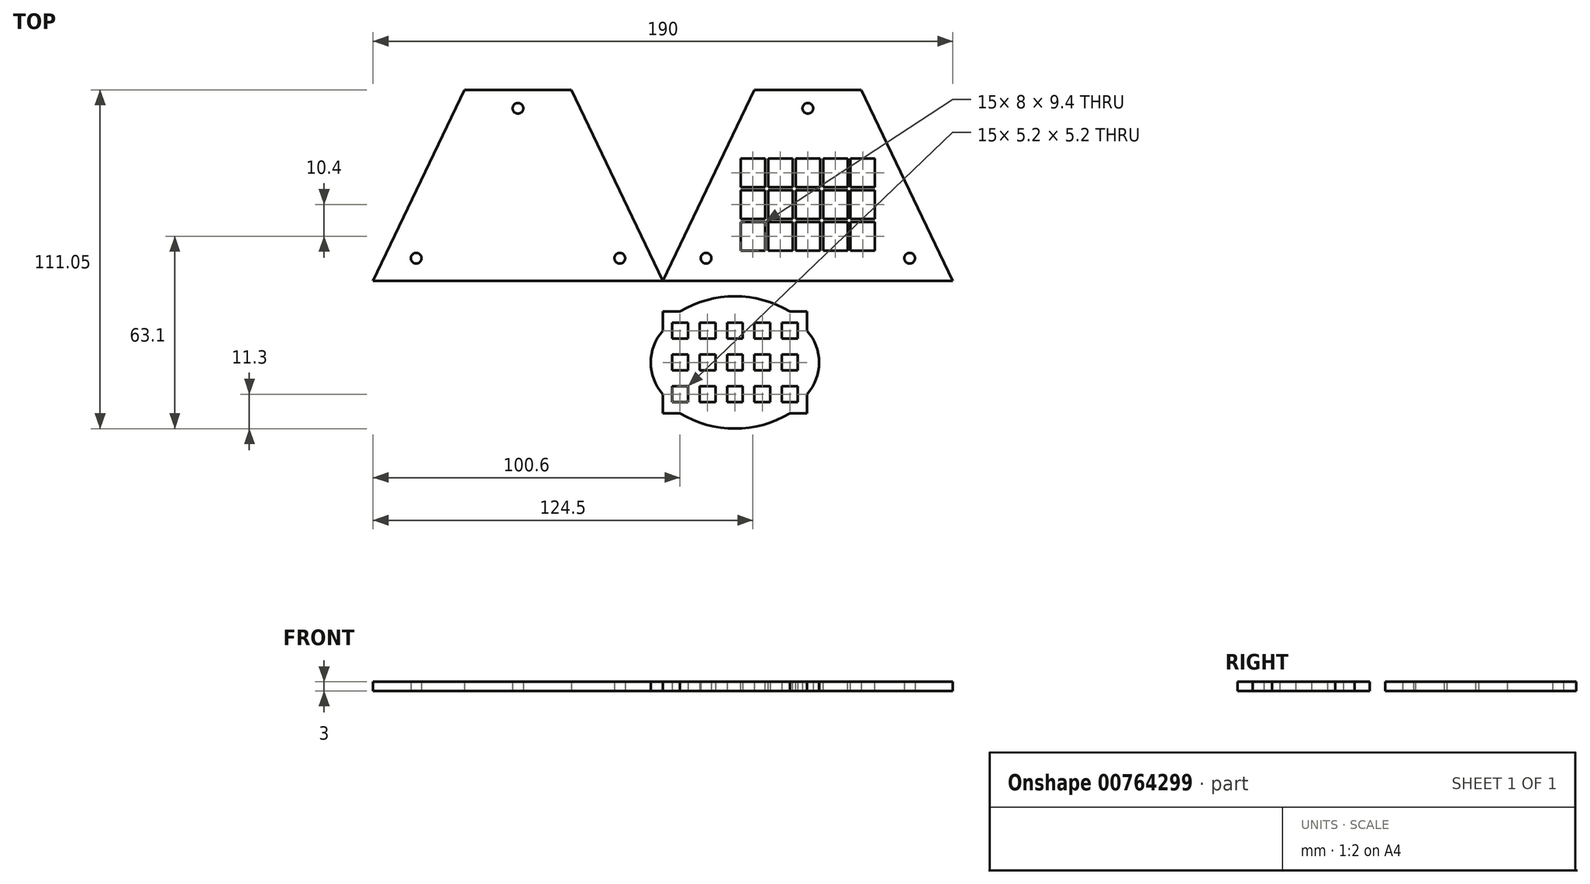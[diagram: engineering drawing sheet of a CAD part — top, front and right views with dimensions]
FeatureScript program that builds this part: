
annotation { "Feature Type Name" : "Feature", "Feature Type Description" : "" }
export const myFeature = defineFeature(function(context is Context, id is Id, definition is map)
    precondition{}
    {
        {
            var Q0;
            Q0=qCreatedBy(makeId("Top.planeOp"),FACE);
            var sketch = newSketch(context, id + "F0", { "sketchPlane" : qUnion([Q0])});
            skLineSegment(sketch, "E0", {"start": v(0, 0) * mm, "end": v(30, 62.65) * mm});
            skLineSegment(sketch, "E1", {"start": v(30, 62.65) * mm, "end": v(65, 62.65) * mm});
            skLineSegment(sketch, "E2", {"start": v(65, 62.65) * mm, "end": v(95, 0) * mm});
            skLineSegment(sketch, "E3", {"start": v(95, 0) * mm, "end": v(0, 0) * mm});
            skLineSegment(sketch, "E4", {"start": v(0, 0) * mm, "end": v(-95, 0) * mm});
            skLineSegment(sketch, "E5", {"start": v(-95, 0) * mm, "end": v(-65, 62.65) * mm});
            skLineSegment(sketch, "E6", {"start": v(-65, 62.65) * mm, "end": v(-30, 62.65) * mm});
            skLineSegment(sketch, "E7", {"start": v(-30, 62.65) * mm, "end": v(0, 0) * mm});
            skCircle(sketch, "E8", {"center": v(-80.86, 7.5) * mm, "radius": 1.75 * mm});
            skCircle(sketch, "E9", {"center": v(-14.14, 7.5) * mm, "radius": 1.75 * mm});
            skCircle(sketch, "E10", {"center": v(14.14, 7.5) * mm, "radius": 1.75 * mm});
            skCircle(sketch, "E11", {"center": v(80.86, 7.5) * mm, "radius": 1.75 * mm});
            skLineSegment(sketch, "E12", {"start": v(-95, 0) * mm, "end": v(-80.86, 7.5) * mm, "construction": true});
            skLineSegment(sketch, "E13", {"start": v(-80.86, 7.5) * mm, "end": v(-14.14, 7.5) * mm, "construction": true});
            skLineSegment(sketch, "E14", {"start": v(-14.14, 7.5) * mm, "end": v(0, 0) * mm, "construction": true});
            skLineSegment(sketch, "E15", {"start": v(0, 0) * mm, "end": v(14.14, 7.5) * mm, "construction": true});
            skLineSegment(sketch, "E16", {"start": v(14.14, 7.5) * mm, "end": v(80.86, 7.5) * mm, "construction": true});
            skLineSegment(sketch, "E17", {"start": v(80.86, 7.5) * mm, "end": v(95, 0) * mm, "construction": true});
            skLineSegment(sketch, "E18", {"start": v(-87.83, 14.98) * mm, "end": v(-80.86, 7.5) * mm, "construction": true});
            skLineSegment(sketch, "E19", {"start": v(-80.86, 7.5) * mm, "end": v(-73.9, 0) * mm, "construction": true});
            skCircle(sketch, "E20", {"center": v(-47.5, 56.65) * mm, "radius": 1.75 * mm});
            skCircle(sketch, "E21", {"center": v(47.5, 56.65) * mm, "radius": 1.75 * mm});
            skLineSegment(sketch, "E22", {"start": v(-47.5, 62.65) * mm, "end": v(-47.5, 56.65) * mm, "construction": true});
            skLineSegment(sketch, "E23", {"start": v(47.5, 62.65) * mm, "end": v(47.5, 56.65) * mm, "construction": true});
            skLineSegment(sketch, "E24.bottom", {"start": v(0, -10) * mm, "end": v(47.2, -10) * mm});
            skLineSegment(sketch, "E24.top", {"start": v(0, -43.4) * mm, "end": v(47.2, -43.4) * mm});
            skLineSegment(sketch, "E24.left", {"start": v(0, -10) * mm, "end": v(0, -43.4) * mm});
            skLineSegment(sketch, "E24.right", {"start": v(47.2, -10) * mm, "end": v(47.2, -43.4) * mm});
            skLineSegment(sketch, "E25.bottom", {"start": v(3, -39.7) * mm, "end": v(8.2, -39.7) * mm});
            skLineSegment(sketch, "E25.top", {"start": v(3, -34.5) * mm, "end": v(8.2, -34.5) * mm});
            skLineSegment(sketch, "E25.left", {"start": v(3, -39.7) * mm, "end": v(3, -34.5) * mm});
            skLineSegment(sketch, "E25.right", {"start": v(8.2, -39.7) * mm, "end": v(8.2, -34.5) * mm});
            skLineSegment(sketch, "E26.0.1.0", {"start": v(3, -29.3) * mm, "end": v(3, -24.1) * mm});
            skLineSegment(sketch, "E26.0.1.1", {"start": v(3, -24.1) * mm, "end": v(8.2, -24.1) * mm});
            skLineSegment(sketch, "E26.0.1.2", {"start": v(8.2, -29.3) * mm, "end": v(8.2, -24.1) * mm});
            skLineSegment(sketch, "E26.0.1.3", {"start": v(3, -29.3) * mm, "end": v(8.2, -29.3) * mm});
            skLineSegment(sketch, "E26.0.2.0", {"start": v(3, -18.9) * mm, "end": v(3, -13.7) * mm});
            skLineSegment(sketch, "E26.0.2.1", {"start": v(3, -13.7) * mm, "end": v(8.2, -13.7) * mm});
            skLineSegment(sketch, "E26.0.2.2", {"start": v(8.2, -18.9) * mm, "end": v(8.2, -13.7) * mm});
            skLineSegment(sketch, "E26.0.2.3", {"start": v(3, -18.9) * mm, "end": v(8.2, -18.9) * mm});
            skLineSegment(sketch, "E26.1.0.0", {"start": v(12, -39.7) * mm, "end": v(12, -34.5) * mm});
            skLineSegment(sketch, "E26.1.0.1", {"start": v(12, -34.5) * mm, "end": v(17.2, -34.5) * mm});
            skLineSegment(sketch, "E26.1.0.2", {"start": v(17.2, -39.7) * mm, "end": v(17.2, -34.5) * mm});
            skLineSegment(sketch, "E26.1.0.3", {"start": v(12, -39.7) * mm, "end": v(17.2, -39.7) * mm});
            skLineSegment(sketch, "E26.1.1.0", {"start": v(12, -29.3) * mm, "end": v(12, -24.1) * mm});
            skLineSegment(sketch, "E26.1.1.1", {"start": v(12, -24.1) * mm, "end": v(17.2, -24.1) * mm});
            skLineSegment(sketch, "E26.1.1.2", {"start": v(17.2, -29.3) * mm, "end": v(17.2, -24.1) * mm});
            skLineSegment(sketch, "E26.1.1.3", {"start": v(12, -29.3) * mm, "end": v(17.2, -29.3) * mm});
            skLineSegment(sketch, "E26.1.2.0", {"start": v(12, -18.9) * mm, "end": v(12, -13.7) * mm});
            skLineSegment(sketch, "E26.1.2.1", {"start": v(12, -13.7) * mm, "end": v(17.2, -13.7) * mm});
            skLineSegment(sketch, "E26.1.2.2", {"start": v(17.2, -18.9) * mm, "end": v(17.2, -13.7) * mm});
            skLineSegment(sketch, "E26.1.2.3", {"start": v(12, -18.9) * mm, "end": v(17.2, -18.9) * mm});
            skLineSegment(sketch, "E26.2.0.0", {"start": v(21, -39.7) * mm, "end": v(21, -34.5) * mm});
            skLineSegment(sketch, "E26.2.0.1", {"start": v(21, -34.5) * mm, "end": v(26.2, -34.5) * mm});
            skLineSegment(sketch, "E26.2.0.2", {"start": v(26.2, -39.7) * mm, "end": v(26.2, -34.5) * mm});
            skLineSegment(sketch, "E26.2.0.3", {"start": v(21, -39.7) * mm, "end": v(26.2, -39.7) * mm});
            skLineSegment(sketch, "E26.2.1.0", {"start": v(21, -29.3) * mm, "end": v(21, -24.1) * mm});
            skLineSegment(sketch, "E26.2.1.1", {"start": v(21, -24.1) * mm, "end": v(26.2, -24.1) * mm});
            skLineSegment(sketch, "E26.2.1.2", {"start": v(26.2, -29.3) * mm, "end": v(26.2, -24.1) * mm});
            skLineSegment(sketch, "E26.2.1.3", {"start": v(21, -29.3) * mm, "end": v(26.2, -29.3) * mm});
            skLineSegment(sketch, "E26.2.2.0", {"start": v(21, -18.9) * mm, "end": v(21, -13.7) * mm});
            skLineSegment(sketch, "E26.2.2.1", {"start": v(21, -13.7) * mm, "end": v(26.2, -13.7) * mm});
            skLineSegment(sketch, "E26.2.2.2", {"start": v(26.2, -18.9) * mm, "end": v(26.2, -13.7) * mm});
            skLineSegment(sketch, "E26.2.2.3", {"start": v(21, -18.9) * mm, "end": v(26.2, -18.9) * mm});
            skLineSegment(sketch, "E26.3.0.0", {"start": v(30, -39.7) * mm, "end": v(30, -34.5) * mm});
            skLineSegment(sketch, "E26.3.0.1", {"start": v(30, -34.5) * mm, "end": v(35.2, -34.5) * mm});
            skLineSegment(sketch, "E26.3.0.2", {"start": v(35.2, -39.7) * mm, "end": v(35.2, -34.5) * mm});
            skLineSegment(sketch, "E26.3.0.3", {"start": v(30, -39.7) * mm, "end": v(35.2, -39.7) * mm});
            skLineSegment(sketch, "E26.3.1.0", {"start": v(30, -29.3) * mm, "end": v(30, -24.1) * mm});
            skLineSegment(sketch, "E26.3.1.1", {"start": v(30, -24.1) * mm, "end": v(35.2, -24.1) * mm});
            skLineSegment(sketch, "E26.3.1.2", {"start": v(35.2, -29.3) * mm, "end": v(35.2, -24.1) * mm});
            skLineSegment(sketch, "E26.3.1.3", {"start": v(30, -29.3) * mm, "end": v(35.2, -29.3) * mm});
            skLineSegment(sketch, "E26.3.2.0", {"start": v(30, -18.9) * mm, "end": v(30, -13.7) * mm});
            skLineSegment(sketch, "E26.3.2.1", {"start": v(30, -13.7) * mm, "end": v(35.2, -13.7) * mm});
            skLineSegment(sketch, "E26.3.2.2", {"start": v(35.2, -18.9) * mm, "end": v(35.2, -13.7) * mm});
            skLineSegment(sketch, "E26.3.2.3", {"start": v(30, -18.9) * mm, "end": v(35.2, -18.9) * mm});
            skLineSegment(sketch, "E26.4.0.0", {"start": v(39, -39.7) * mm, "end": v(39, -34.5) * mm});
            skLineSegment(sketch, "E26.4.0.1", {"start": v(39, -34.5) * mm, "end": v(44.2, -34.5) * mm});
            skLineSegment(sketch, "E26.4.0.2", {"start": v(44.2, -39.7) * mm, "end": v(44.2, -34.5) * mm});
            skLineSegment(sketch, "E26.4.0.3", {"start": v(39, -39.7) * mm, "end": v(44.2, -39.7) * mm});
            skLineSegment(sketch, "E26.4.1.0", {"start": v(39, -29.3) * mm, "end": v(39, -24.1) * mm});
            skLineSegment(sketch, "E26.4.1.1", {"start": v(39, -24.1) * mm, "end": v(44.2, -24.1) * mm});
            skLineSegment(sketch, "E26.4.1.2", {"start": v(44.2, -29.3) * mm, "end": v(44.2, -24.1) * mm});
            skLineSegment(sketch, "E26.4.1.3", {"start": v(39, -29.3) * mm, "end": v(44.2, -29.3) * mm});
            skLineSegment(sketch, "E26.4.2.0", {"start": v(39, -18.9) * mm, "end": v(39, -13.7) * mm});
            skLineSegment(sketch, "E26.4.2.1", {"start": v(39, -13.7) * mm, "end": v(44.2, -13.7) * mm});
            skLineSegment(sketch, "E26.4.2.2", {"start": v(44.2, -18.9) * mm, "end": v(44.2, -13.7) * mm});
            skLineSegment(sketch, "E26.4.2.3", {"start": v(39, -18.9) * mm, "end": v(44.2, -18.9) * mm});
            skLineSegment(sketch, "E26.direction1", {"start": v(3, -39.7) * mm, "end": v(12, -39.7) * mm, "construction": true});
            skLineSegment(sketch, "E26.direction2", {"start": v(3, -39.7) * mm, "end": v(3, -29.3) * mm, "construction": true});
            skLineSegment(sketch, "E27", {"start": v(23.6, -39.7) * mm, "end": v(23.6, -43.4) * mm, "construction": true});
            skLineSegment(sketch, "E28", {"start": v(0, -26.7) * mm, "end": v(3, -26.7) * mm, "construction": true});
            skArc(sketch, "E29", {"start": v(41.6, -10) * mm, "mid": v(23.6, -5) * mm, "end": v(5.6, -10) * mm});
            skArc(sketch, "E30", {"start": v(5.6, -43.4) * mm, "mid": v(23.6, -48.4) * mm, "end": v(41.6, -43.4) * mm});
            skArc(sketch, "E31", {"start": v(47.2, -37.1) * mm, "mid": v(51.2, -26.7) * mm, "end": v(47.2, -16.3) * mm});
            skArc(sketch, "E32", {"start": v(0, -16.3) * mm, "mid": v(-4, -26.7) * mm, "end": v(0, -37.1) * mm});
            skLineSegment(sketch, "E33", {"start": v(0, -16.3) * mm, "end": v(3, -16.3) * mm, "construction": true});
            skLineSegment(sketch, "E34", {"start": v(5.6, -13.7) * mm, "end": v(5.6, -10) * mm, "construction": true});
            skLineSegment(sketch, "E35", {"start": v(11.52, -26.7) * mm, "end": v(23.6, -26.7) * mm, "construction": true});
            skLineSegment(sketch, "E36", {"start": v(23.6, -26.7) * mm, "end": v(35.68, -26.7) * mm, "construction": true});
            skLineSegment(sketch, "E37", {"start": v(41.6, -13.7) * mm, "end": v(41.6, -10) * mm, "construction": true});
            skLineSegment(sketch, "E38", {"start": v(0, -37.1) * mm, "end": v(3, -37.1) * mm, "construction": true});
            skPoint(sketch, "E39", {"position": v(23.6, -18.9) * mm});
            skLineSegment(sketch, "E40", {"start": v(23.6, -13.5) * mm, "end": v(23.6, -26.7) * mm, "construction": true});
            skLineSegment(sketch, "E41", {"start": v(23.6, -26.7) * mm, "end": v(23.6, -39.9) * mm, "construction": true});
            skSolve(sketch);
        }
        {
            var Q0;
            Q0=makeQuery(id+"F0.imprint","IMPRINT",FACE,{"disambiguationData":[TD([[makeQuery(id+"F0.imprint","IMPRINT",EDGE,{"derivedFrom":sQuery(id+"F0.wireOp",EDGE,"E4")}),-1.0]])]});
            var Q1;
            Q1=makeQuery(id+"F0.imprint","IMPRINT",FACE,{"disambiguationData":[TD([[makeQuery(id+"F0.imprint","IMPRINT",EDGE,{"derivedFrom":sQuery(id+"F0.wireOp",EDGE,"E0")}),-1.0]])]});
            var Q2;
            Q2=makeQuery(id+"F0.imprint","IMPRINT",FACE,{"disambiguationData":[TD([[makeQuery(id+"F0.imprint","IMPRINT",EDGE,{"derivedFrom":sQuery(id+"F0.wireOp",EDGE,"E24.bottom")}),-1.0]])]});
            var Q3;
            {var subQ0=sQuery(id+"F0.wireOp",EDGE,"E30");Q3=makeQuery(id+"F0.imprint","IMPRINT",FACE,{"disambiguationData":[TD([[makeQuery(id+"F0.imprint","IMPRINT",EDGE,{"derivedFrom":subQ0}),1.0]])]});}
            var Q4;
            {var subQ0=sQuery(id+"F0.wireOp",EDGE,"E31");Q4=makeQuery(id+"F0.imprint","IMPRINT",FACE,{"disambiguationData":[TD([[makeQuery(id+"F0.imprint","IMPRINT",EDGE,{"derivedFrom":subQ0}),1.0]])]});}
            var Q5;
            {var subQ0=sQuery(id+"F0.wireOp",EDGE,"E29");Q5=makeQuery(id+"F0.imprint","IMPRINT",FACE,{"disambiguationData":[TD([[makeQuery(id+"F0.imprint","IMPRINT",EDGE,{"derivedFrom":subQ0}),1.0]])]});}
            var Q6;
            {var subQ0=sQuery(id+"F0.wireOp",EDGE,"E32");Q6=makeQuery(id+"F0.imprint","IMPRINT",FACE,{"disambiguationData":[TD([[makeQuery(id+"F0.imprint","IMPRINT",EDGE,{"derivedFrom":subQ0}),1.0]])]});}
            extrude(context, id + "F1", {"entities" : qUnion([Q0, Q1, Q2, Q3, Q4, Q5, Q6]), "depth" : 3 * mm, "offsetDistance" : 25 * mm});
        }
        {
            var Q0;
            Q0=makeQuery(id+"F1.opExtrude","CAP_FACE",FACE,{"disambiguationData":[OSD([sQuery(id+"F0.wireOp",EDGE,"E0"),sQuery(id+"F0.wireOp",EDGE,"E1"),sQuery(id+"F0.wireOp",EDGE,"E2"),sQuery(id+"F0.wireOp",EDGE,"E3"),sQuery(id+"F0.wireOp",EDGE,"E10"),sQuery(id+"F0.wireOp",EDGE,"E11"),sQuery(id+"F0.wireOp",EDGE,"E21")])],"isStart":false});
            var sketch = newSketch(context, id + "F2", { "sketchPlane" : qUnion([Q0])});
            skLineSegment(sketch, "E42.bottom", {"start": v(25.5, 19.4) * mm, "end": v(33.5, 19.4) * mm});
            skLineSegment(sketch, "E42.top", {"start": v(25.5, 10) * mm, "end": v(33.5, 10) * mm});
            skLineSegment(sketch, "E42.left", {"start": v(25.5, 19.4) * mm, "end": v(25.5, 10) * mm});
            skLineSegment(sketch, "E42.right", {"start": v(33.5, 19.4) * mm, "end": v(33.5, 10) * mm});
            skLineSegment(sketch, "E43.0.1.0", {"start": v(25.5, 29.8) * mm, "end": v(33.5, 29.8) * mm});
            skLineSegment(sketch, "E43.0.1.1", {"start": v(25.5, 29.8) * mm, "end": v(25.5, 20.4) * mm});
            skLineSegment(sketch, "E43.0.1.2", {"start": v(25.5, 20.4) * mm, "end": v(33.5, 20.4) * mm});
            skLineSegment(sketch, "E43.0.1.3", {"start": v(33.5, 29.8) * mm, "end": v(33.5, 20.4) * mm});
            skLineSegment(sketch, "E43.0.2.0", {"start": v(25.5, 40.2) * mm, "end": v(33.5, 40.2) * mm});
            skLineSegment(sketch, "E43.0.2.1", {"start": v(25.5, 40.2) * mm, "end": v(25.5, 30.8) * mm});
            skLineSegment(sketch, "E43.0.2.2", {"start": v(25.5, 30.8) * mm, "end": v(33.5, 30.8) * mm});
            skLineSegment(sketch, "E43.0.2.3", {"start": v(33.5, 40.2) * mm, "end": v(33.5, 30.8) * mm});
            skLineSegment(sketch, "E43.1.0.0", {"start": v(34.5, 19.4) * mm, "end": v(42.5, 19.4) * mm});
            skLineSegment(sketch, "E43.1.0.1", {"start": v(34.5, 19.4) * mm, "end": v(34.5, 10) * mm});
            skLineSegment(sketch, "E43.1.0.2", {"start": v(34.5, 10) * mm, "end": v(42.5, 10) * mm});
            skLineSegment(sketch, "E43.1.0.3", {"start": v(42.5, 19.4) * mm, "end": v(42.5, 10) * mm});
            skLineSegment(sketch, "E43.1.1.0", {"start": v(34.5, 29.8) * mm, "end": v(42.5, 29.8) * mm});
            skLineSegment(sketch, "E43.1.1.1", {"start": v(34.5, 29.8) * mm, "end": v(34.5, 20.4) * mm});
            skLineSegment(sketch, "E43.1.1.2", {"start": v(34.5, 20.4) * mm, "end": v(42.5, 20.4) * mm});
            skLineSegment(sketch, "E43.1.1.3", {"start": v(42.5, 29.8) * mm, "end": v(42.5, 20.4) * mm});
            skLineSegment(sketch, "E43.1.2.0", {"start": v(34.5, 40.2) * mm, "end": v(42.5, 40.2) * mm});
            skLineSegment(sketch, "E43.1.2.1", {"start": v(34.5, 40.2) * mm, "end": v(34.5, 30.8) * mm});
            skLineSegment(sketch, "E43.1.2.2", {"start": v(34.5, 30.8) * mm, "end": v(42.5, 30.8) * mm});
            skLineSegment(sketch, "E43.1.2.3", {"start": v(42.5, 40.2) * mm, "end": v(42.5, 30.8) * mm});
            skLineSegment(sketch, "E43.2.0.0", {"start": v(43.5, 19.4) * mm, "end": v(51.5, 19.4) * mm});
            skLineSegment(sketch, "E43.2.0.1", {"start": v(43.5, 19.4) * mm, "end": v(43.5, 10) * mm});
            skLineSegment(sketch, "E43.2.0.2", {"start": v(43.5, 10) * mm, "end": v(51.5, 10) * mm});
            skLineSegment(sketch, "E43.2.0.3", {"start": v(51.5, 19.4) * mm, "end": v(51.5, 10) * mm});
            skLineSegment(sketch, "E43.2.1.0", {"start": v(43.5, 29.8) * mm, "end": v(51.5, 29.8) * mm});
            skLineSegment(sketch, "E43.2.1.1", {"start": v(43.5, 29.8) * mm, "end": v(43.5, 20.4) * mm});
            skLineSegment(sketch, "E43.2.1.2", {"start": v(43.5, 20.4) * mm, "end": v(51.5, 20.4) * mm});
            skLineSegment(sketch, "E43.2.1.3", {"start": v(51.5, 29.8) * mm, "end": v(51.5, 20.4) * mm});
            skLineSegment(sketch, "E43.2.2.0", {"start": v(43.5, 40.2) * mm, "end": v(51.5, 40.2) * mm});
            skLineSegment(sketch, "E43.2.2.1", {"start": v(43.5, 40.2) * mm, "end": v(43.5, 30.8) * mm});
            skLineSegment(sketch, "E43.2.2.2", {"start": v(43.5, 30.8) * mm, "end": v(51.5, 30.8) * mm});
            skLineSegment(sketch, "E43.2.2.3", {"start": v(51.5, 40.2) * mm, "end": v(51.5, 30.8) * mm});
            skLineSegment(sketch, "E43.direction1", {"start": v(25.5, 10) * mm, "end": v(34.5, 10) * mm, "construction": true});
            skLineSegment(sketch, "E43.direction2", {"start": v(25.5, 10) * mm, "end": v(25.5, 20.4) * mm, "construction": true});
            skLineSegment(sketch, "E44.0.3.0", {"start": v(52.5, 19.4) * mm, "end": v(60.5, 19.4) * mm});
            skLineSegment(sketch, "E44.3.3.0", {"start": v(52.5, 19.4) * mm, "end": v(52.5, 10) * mm});
            skLineSegment(sketch, "E44.6.3.0", {"start": v(52.5, 10) * mm, "end": v(60.5, 10) * mm});
            skLineSegment(sketch, "E44.9.3.0", {"start": v(60.5, 19.4) * mm, "end": v(60.5, 10) * mm});
            skLineSegment(sketch, "E44.0.3.1", {"start": v(52.5, 29.8) * mm, "end": v(60.5, 29.8) * mm});
            skLineSegment(sketch, "E44.3.3.1", {"start": v(52.5, 29.8) * mm, "end": v(52.5, 20.4) * mm});
            skLineSegment(sketch, "E44.6.3.1", {"start": v(52.5, 20.4) * mm, "end": v(60.5, 20.4) * mm});
            skLineSegment(sketch, "E44.9.3.1", {"start": v(60.5, 29.8) * mm, "end": v(60.5, 20.4) * mm});
            skLineSegment(sketch, "E44.0.3.2", {"start": v(52.5, 40.2) * mm, "end": v(60.5, 40.2) * mm});
            skLineSegment(sketch, "E44.3.3.2", {"start": v(52.5, 40.2) * mm, "end": v(52.5, 30.8) * mm});
            skLineSegment(sketch, "E44.6.3.2", {"start": v(52.5, 30.8) * mm, "end": v(60.5, 30.8) * mm});
            skLineSegment(sketch, "E44.9.3.2", {"start": v(60.5, 40.2) * mm, "end": v(60.5, 30.8) * mm});
            skLineSegment(sketch, "E44.0.4.0", {"start": v(61.5, 19.4) * mm, "end": v(69.5, 19.4) * mm});
            skLineSegment(sketch, "E44.3.4.0", {"start": v(61.5, 19.4) * mm, "end": v(61.5, 10) * mm});
            skLineSegment(sketch, "E44.6.4.0", {"start": v(61.5, 10) * mm, "end": v(69.5, 10) * mm});
            skLineSegment(sketch, "E44.9.4.0", {"start": v(69.5, 19.4) * mm, "end": v(69.5, 10) * mm});
            skLineSegment(sketch, "E44.0.4.1", {"start": v(61.5, 29.8) * mm, "end": v(69.5, 29.8) * mm});
            skLineSegment(sketch, "E44.3.4.1", {"start": v(61.5, 29.8) * mm, "end": v(61.5, 20.4) * mm});
            skLineSegment(sketch, "E44.6.4.1", {"start": v(61.5, 20.4) * mm, "end": v(69.5, 20.4) * mm});
            skLineSegment(sketch, "E44.9.4.1", {"start": v(69.5, 29.8) * mm, "end": v(69.5, 20.4) * mm});
            skLineSegment(sketch, "E44.0.4.2", {"start": v(61.5, 40.2) * mm, "end": v(69.5, 40.2) * mm});
            skLineSegment(sketch, "E44.3.4.2", {"start": v(61.5, 40.2) * mm, "end": v(61.5, 30.8) * mm});
            skLineSegment(sketch, "E44.6.4.2", {"start": v(61.5, 30.8) * mm, "end": v(69.5, 30.8) * mm});
            skLineSegment(sketch, "E44.9.4.2", {"start": v(69.5, 40.2) * mm, "end": v(69.5, 30.8) * mm});
            skLineSegment(sketch, "E45", {"start": v(47.5, 10) * mm, "end": v(47.5, 0) * mm, "construction": true});
            skSolve(sketch);
        }
        {
            var Q0;
            Q0 = qSketchRegion(id + "F2", true);
            extrude(context, id + "F3", {"entities" : qUnion([Q0]), "operationType" : NewBodyOperationType.REMOVE, "endBound" : BoundingType.THROUGH_ALL, "oppositeDirection" : true, "depth" : 25 * mm, "offsetDistance" : 25 * mm});
        }
    });
